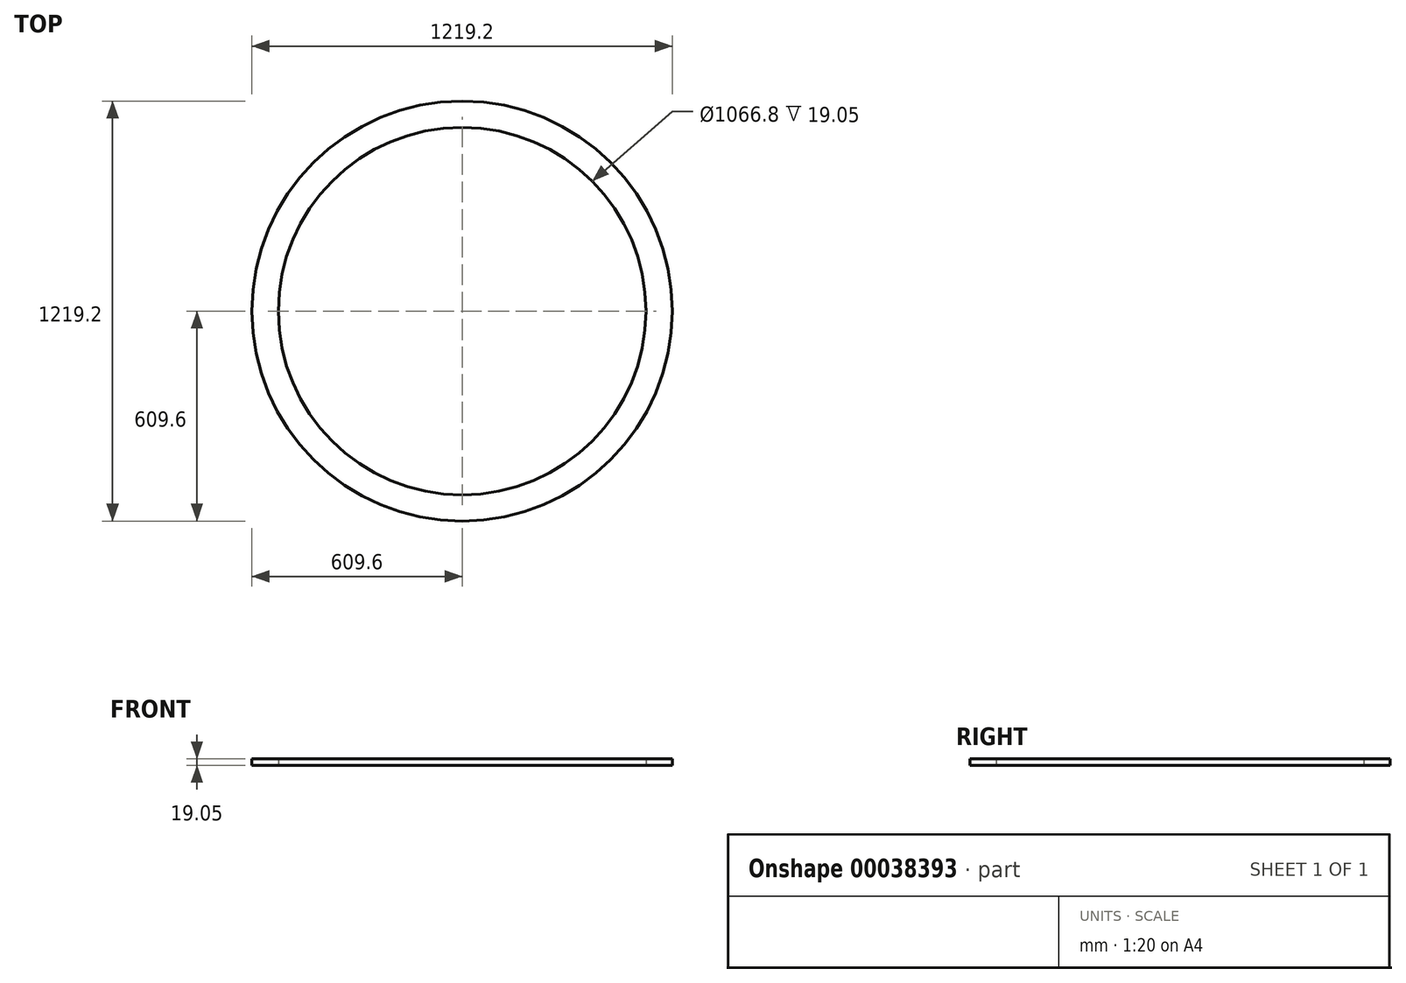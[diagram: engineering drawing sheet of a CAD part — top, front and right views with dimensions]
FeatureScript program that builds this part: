
annotation { "Feature Type Name" : "Feature", "Feature Type Description" : "" }
export const myFeature = defineFeature(function(context is Context, id is Id, definition is map)
    precondition{}
    {
        {
            var Q0;
            Q0=qCreatedBy(makeId("Top.planeOp"),FACE);
            var sketch = newSketch(context, id + "F0", { "sketchPlane" : qUnion([Q0])});
            skCircle(sketch, "E0", {"center": v(0, 0) * mm, "radius": 609.6 * mm});
            skCircle(sketch, "E1", {"center": v(0, 0) * mm, "radius": 533.4 * mm});
            skLineSegment(sketch, "E2", {"start": v(0, 0) * mm, "end": v(533.4, 0) * mm, "construction": true});
            skLineSegment(sketch, "E3.0", {"start": v(0, -65.7) * mm, "end": v(533.4, -65.7) * mm, "construction": true});
            skLineSegment(sketch, "E4.0", {"start": v(0, 30.6) * mm, "end": v(533.4, 30.6) * mm, "construction": true});
            skSolve(sketch);
        }
        {
            var Q0;
            Q0=makeQuery(id+"F0.imprint","IMPRINT",FACE,{"disambiguationData":[TD([[makeQuery(id+"F0.imprint","IMPRINT",EDGE,{"derivedFrom":sQuery(id+"F0.wireOp",EDGE,"E0")}),1.0]])]});
            extrude(context, id + "F1", {"entities" : qUnion([Q0]), "depth" : 19.05 * mm});
        }
    });
